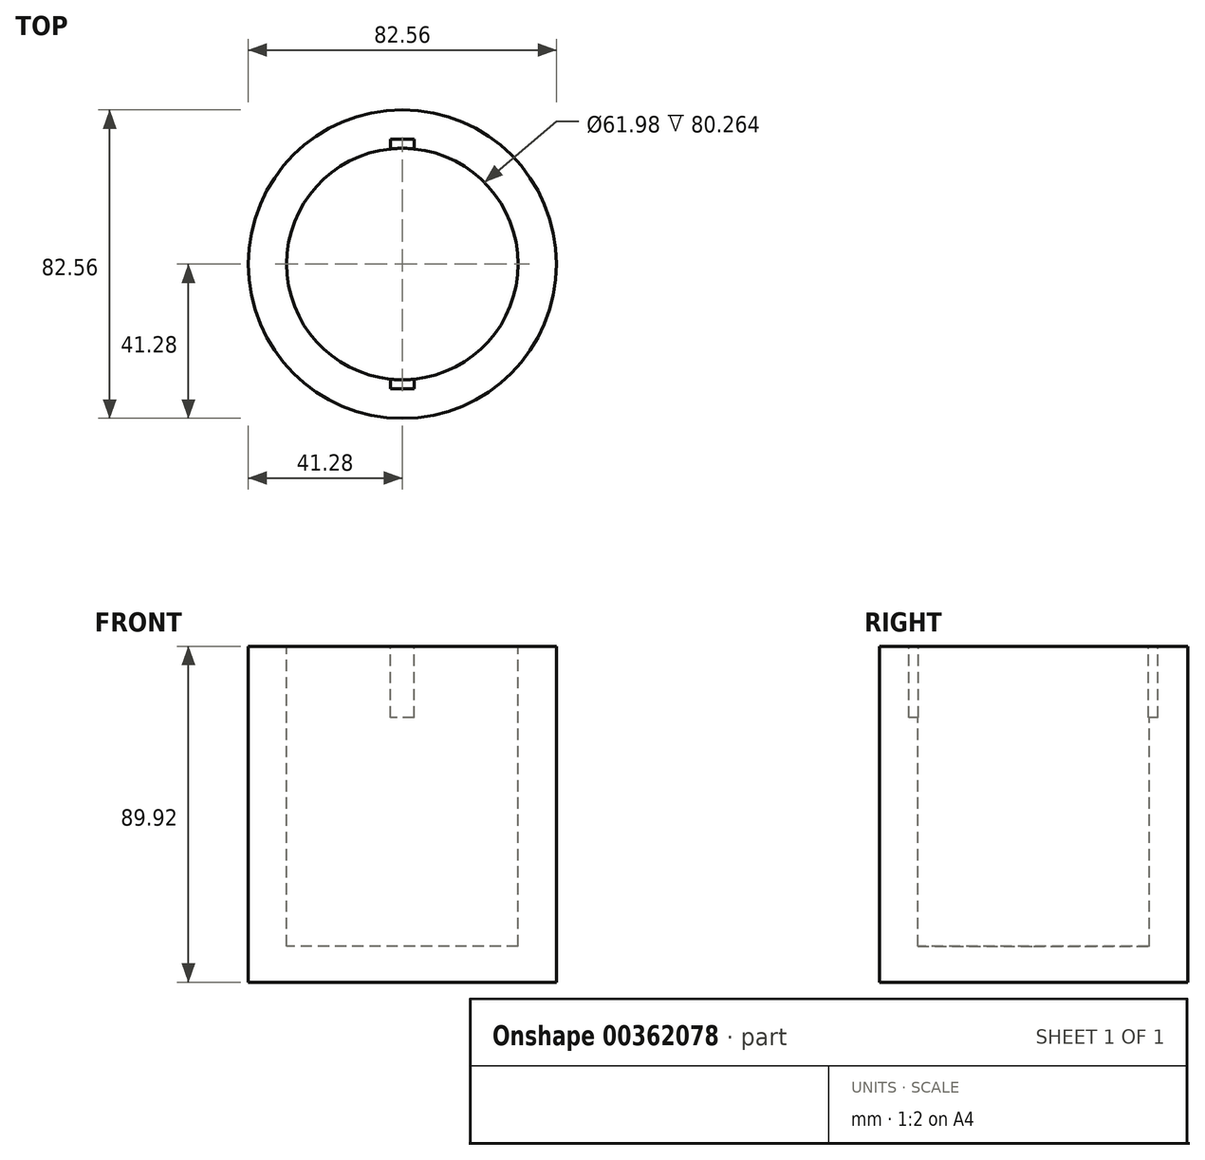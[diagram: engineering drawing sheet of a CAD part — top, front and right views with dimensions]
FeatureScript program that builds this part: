
annotation { "Feature Type Name" : "Feature", "Feature Type Description" : "" }
export const myFeature = defineFeature(function(context is Context, id is Id, definition is map)
    precondition{}
    {
        {
            var Q0;
            Q0=qCreatedBy(makeId("Top.planeOp"),FACE);
            var sketch = newSketch(context, id + "F0", { "sketchPlane" : qUnion([Q0])});
            skCircle(sketch, "E0", {"center": v(0, 0) * mm, "radius": 41.28 * mm});
            skSolve(sketch);
        }
        {
            var Q0;
            Q0 = qSketchRegion(id + "F0", true);
            extrude(context, id + "F1", {"entities" : qUnion([Q0]), "depth" : 89.92 * mm});
        }
        {
            var Q0;
            Q0=makeQuery(id+"F1.opExtrude","CAP_FACE",FACE,{"disambiguationData":[OSD([sQuery(id+"F0.wireOp",EDGE,"E0")])],"isStart":false});
            var sketch = newSketch(context, id + "F2", { "sketchPlane" : qUnion([Q0])});
            skCircle(sketch, "E1", {"center": v(0, 0) * mm, "radius": 30.99 * mm});
            skSolve(sketch);
        }
        {
            var Q0;
            Q0 = qSketchRegion(id + "F2", true);
            extrude(context, id + "F3", {"entities" : qUnion([Q0]), "operationType" : NewBodyOperationType.REMOVE, "oppositeDirection" : true, "depth" : 80.26 * mm});
        }
        {
            var Q0;
            Q0=makeQuery(id+"F1.opExtrude","CAP_FACE",FACE,{"disambiguationData":[OSD([sQuery(id+"F0.wireOp",EDGE,"E0")])],"isStart":false});
            var sketch = newSketch(context, id + "F4", { "sketchPlane" : qUnion([Q0])});
            skLineSegment(sketch, "E2", {"start": v(0, 41.28) * mm, "end": v(0, -41.28) * mm, "construction": true});
            skLineSegment(sketch, "E3", {"start": v(-41.28, 0) * mm, "end": v(41.28, 0) * mm, "construction": true});
            skLineSegment(sketch, "E4", {"start": v(0, 33.37) * mm, "end": v(-3.17, 33.37) * mm});
            skLineSegment(sketch, "E5", {"start": v(-3.17, 33.37) * mm, "end": v(-3.17, 0) * mm});
            skLineSegment(sketch, "E6.MirrorCS", {"start": v(3.18, 33.37) * mm, "end": v(3.18, 0) * mm});
            skLineSegment(sketch, "E7.MirrorCS", {"start": v(0, 33.37) * mm, "end": v(3.18, 33.37) * mm});
            skLineSegment(sketch, "E8.MirrorCS", {"start": v(3.18, -33.37) * mm, "end": v(3.18, 0) * mm});
            skLineSegment(sketch, "E9.MirrorCS", {"start": v(-3.17, -33.37) * mm, "end": v(-3.17, 0) * mm});
            skLineSegment(sketch, "E10.MirrorCS", {"start": v(0, -33.37) * mm, "end": v(3.18, -33.37) * mm});
            skLineSegment(sketch, "E11.MirrorCS", {"start": v(0, -33.37) * mm, "end": v(-3.17, -33.37) * mm});
            skSolve(sketch);
        }
        {
            var Q0;
            Q0 = qSketchRegion(id + "F4", true);
            extrude(context, id + "F5", {"entities" : qUnion([Q0]), "operationType" : NewBodyOperationType.REMOVE, "oppositeDirection" : true, "depth" : 19.05 * mm});
        }
    });
